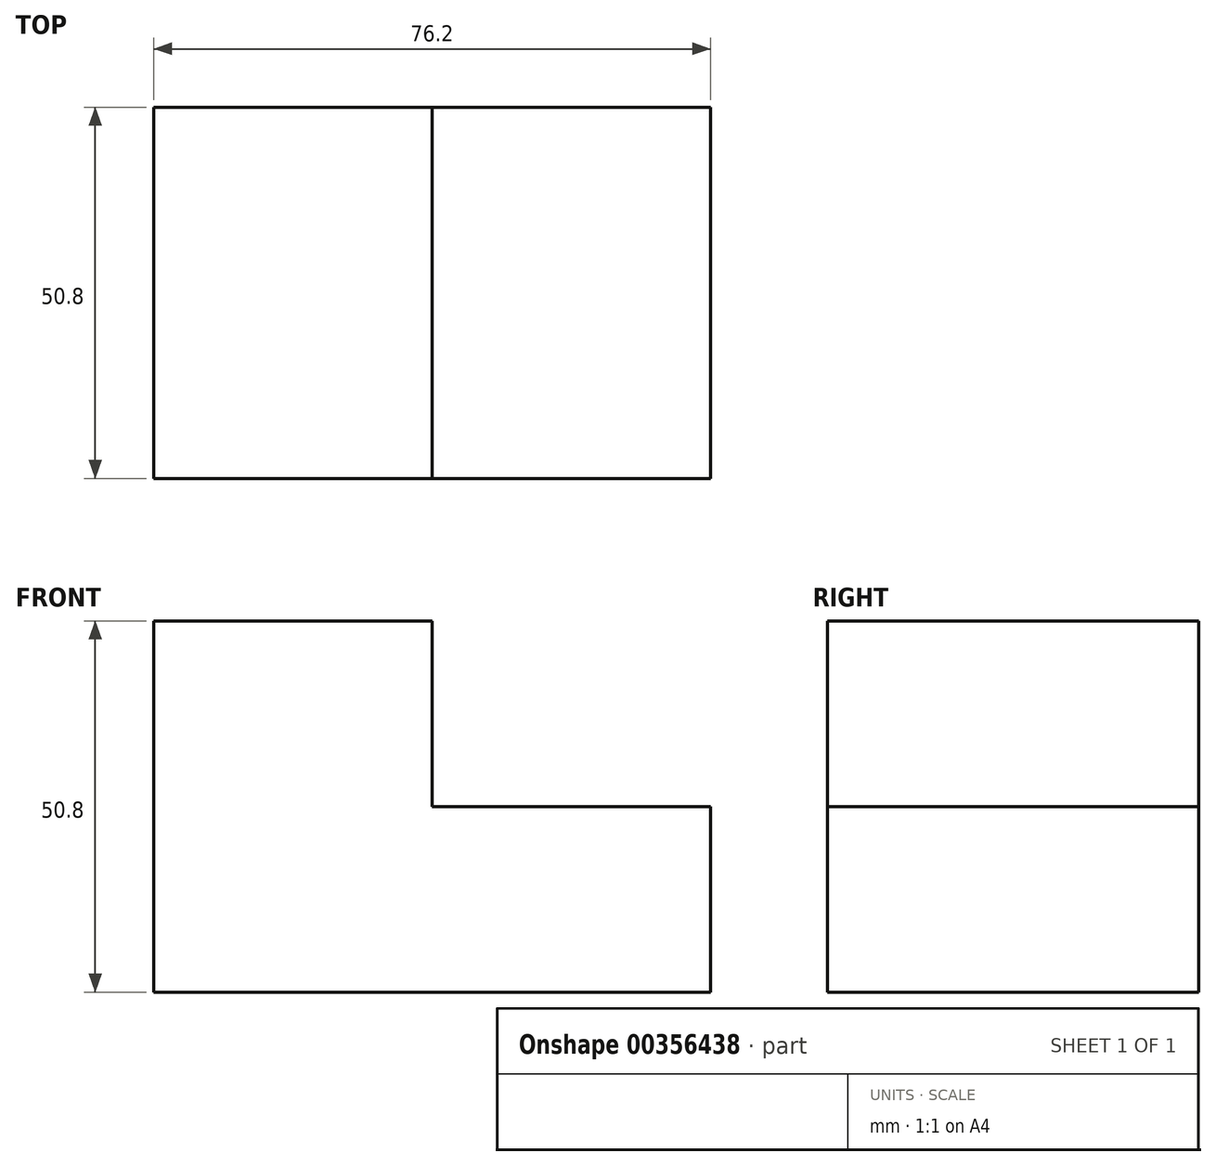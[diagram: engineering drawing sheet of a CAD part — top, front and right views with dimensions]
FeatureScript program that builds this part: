
annotation { "Feature Type Name" : "Feature", "Feature Type Description" : "" }
export const myFeature = defineFeature(function(context is Context, id is Id, definition is map)
    precondition{}
    {
        {
            var Q0;
            Q0=qCreatedBy(makeId("Front.planeOp"),FACE);
            var sketch = newSketch(context, id + "F0", { "sketchPlane" : qUnion([Q0])});
            skLineSegment(sketch, "E0", {"start": v(-46.38, 57.34) * mm, "end": v(-46.38, 6.54) * mm});
            skLineSegment(sketch, "E1", {"start": v(-46.38, 6.54) * mm, "end": v(29.82, 6.54) * mm});
            skLineSegment(sketch, "E2", {"start": v(29.82, 6.54) * mm, "end": v(29.82, 31.94) * mm});
            skLineSegment(sketch, "E3", {"start": v(29.82, 31.94) * mm, "end": v(-8.28, 31.94) * mm});
            skLineSegment(sketch, "E4", {"start": v(-8.28, 31.94) * mm, "end": v(-8.28, 57.34) * mm});
            skLineSegment(sketch, "E5", {"start": v(-8.28, 57.34) * mm, "end": v(-46.38, 57.34) * mm});
            skSolve(sketch);
        }
        {
            var Q0;
            Q0=makeQuery(id+"F0.imprint","IMPRINT",FACE,{"disambiguationData":[TD([[makeQuery(id+"F0.imprint","IMPRINT",EDGE,{"derivedFrom":sQuery(id+"F0.wireOp",EDGE,"E0")}),1.0]])]});
            extrude(context, id + "F1", {"entities" : qUnion([Q0]), "depth" : 50.8 * mm});
        }
    });
